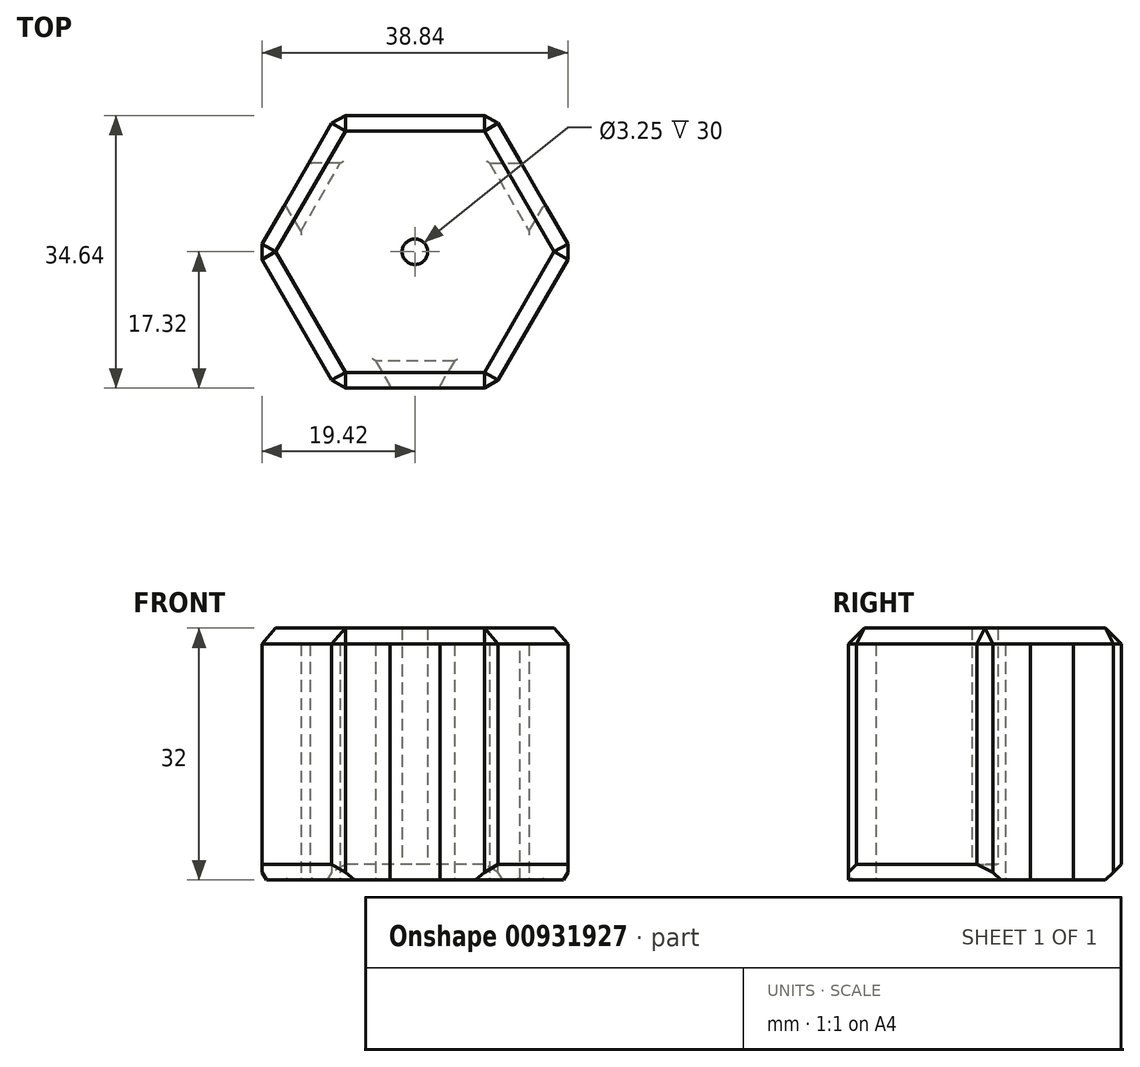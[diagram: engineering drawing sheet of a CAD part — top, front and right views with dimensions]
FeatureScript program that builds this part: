
annotation { "Feature Type Name" : "Feature", "Feature Type Description" : "" }
export const myFeature = defineFeature(function(context is Context, id is Id, definition is map)
    precondition{}
    {
        {
            var Q0;
            Q0=qCreatedBy(makeId("Top.planeOp"),FACE);
            var sketch = newSketch(context, id + "F0", { "sketchPlane" : qUnion([Q0])});
            skCircle(sketch, "E0.cCircle", {"center": v(0, 0) * mm, "radius": 17.32 * mm, "construction": true});
            skLineSegment(sketch, "E0.0", {"start": v(-20, 0) * mm, "end": v(-10, 17.32) * mm});
            skLineSegment(sketch, "E0.1", {"start": v(-10, 17.32) * mm, "end": v(10, 17.32) * mm});
            skLineSegment(sketch, "E0.2", {"start": v(10, 17.32) * mm, "end": v(20, 0) * mm});
            skLineSegment(sketch, "E0.3", {"start": v(20, 0) * mm, "end": v(10, -17.32) * mm});
            skLineSegment(sketch, "E0.4", {"start": v(10, -17.32) * mm, "end": v(-10, -17.32) * mm});
            skLineSegment(sketch, "E0.5", {"start": v(-10, -17.32) * mm, "end": v(-20, 0) * mm});
            skPoint(sketch, "E0.0.midPoint", {"position": v(-15, 8.66) * mm});
            skLineSegment(sketch, "E1", {"start": v(9.5, 11.26) * mm, "end": v(14.5, 2.6) * mm});
            skLineSegment(sketch, "E2", {"start": v(9.5, 11.26) * mm, "end": v(13.5, 11.26) * mm});
            skLineSegment(sketch, "E3", {"start": v(14.5, 2.6) * mm, "end": v(16.5, 6.06) * mm});
            skLineSegment(sketch, "E4", {"start": v(13.5, 11.26) * mm, "end": v(10, 17.32) * mm, "construction": true});
            skLineSegment(sketch, "E5", {"start": v(16.5, 6.06) * mm, "end": v(20, 0) * mm, "construction": true});
            skLineSegment(sketch, "E6.1.0", {"start": v(-9.5, 11.26) * mm, "end": v(-13.5, 11.26) * mm});
            skLineSegment(sketch, "E6.1.1", {"start": v(-14.5, 2.6) * mm, "end": v(-9.5, 11.26) * mm});
            skLineSegment(sketch, "E6.1.2", {"start": v(-14.5, 2.6) * mm, "end": v(-16.5, 6.06) * mm});
            skLineSegment(sketch, "E6.2.0", {"start": v(-5, -13.86) * mm, "end": v(-3, -17.32) * mm});
            skLineSegment(sketch, "E6.2.1", {"start": v(5, -13.86) * mm, "end": v(-5, -13.86) * mm});
            skLineSegment(sketch, "E6.2.2", {"start": v(5, -13.86) * mm, "end": v(3, -17.32) * mm});
            skCircle(sketch, "E7", {"center": v(0, 0) * mm, "radius": 1.63 * mm});
            skSolve(sketch);
        }
        {
            var Q0;
            {var subQ9=sQuery(id+"F0.wireOp",EDGE,"E0.1");Q0=makeQuery(id+"F0.imprint","IMPRINT",FACE,{"disambiguationData":[TD([[makeQuery(id+"F0.imprint","IMPRINT",EDGE,{"derivedFrom":subQ9}),-1.0]])]});}
            extrude(context, id + "F1", {"entities" : qUnion([Q0]), "depth" : 32 * mm, "offsetDistance" : 25 * mm});
        }
        {
            var Q0;
            {var subQ0=sQuery(id+"F0.wireOp",EDGE,"E6.2.0");Q0=makeQuery(id+"F0.imprint","IMPRINT",FACE,{"disambiguationData":[TD([[makeQuery(id+"F0.imprint","IMPRINT",EDGE,{"derivedFrom":subQ0}),1.0]])]});}
            var Q1;
            {var subQ0=sQuery(id+"F0.wireOp",EDGE,"E6.1.0");Q1=makeQuery(id+"F0.imprint","IMPRINT",FACE,{"disambiguationData":[TD([[makeQuery(id+"F0.imprint","IMPRINT",EDGE,{"derivedFrom":subQ0}),1.0]])]});}
            var Q2;
            Q2=makeQuery(id+"F0.imprint","IMPRINT",FACE,{"disambiguationData":[TD([[makeQuery(id+"F0.imprint","IMPRINT",EDGE,{"derivedFrom":sQuery(id+"F0.wireOp",EDGE,"E1")}),1.0]])]});
            extrude(context, id + "F2", {"entities" : qUnion([Q0, Q1, Q2]), "operationType" : NewBodyOperationType.ADD, "depth" : 32 * mm, "offsetDistance" : 25 * mm, "hasSecondDirection" : true, "secondDirectionOppositeDirection" : false, "secondDirectionDepth" : 30 * mm});
        }
        {
            var Q0;
            Q0=makeQuery(id+"F1.opExtrude","CAP_EDGE",EDGE,{"disambiguationData":[OSD([sQuery(id+"F0.wireOp",EDGE,"E0.3")])],"isStart":false});
            var Q1;
            Q1=makeQuery(id+"F1.opExtrude","CAP_EDGE",EDGE,{"disambiguationData":[OSD([sQuery(id+"F0.wireOp",EDGE,"E0.5")])],"isStart":false});
            var Q2;
            Q2=makeQuery(id+"F1.opExtrude","CAP_EDGE",EDGE,{"disambiguationData":[OSD([sQuery(id+"F0.wireOp",EDGE,"E0.1")])],"isStart":false});
            var Q3;
            {var subQ0=sQuery(id+"F0.wireOp",EDGE,"E0.4");Q3=makeQuery(id+"F1.opExtrude","CAP_EDGE",EDGE,{"disambiguationData":[OSD([subQ0]),TDD([makeQuery(id+"F0.imprint","IMPRINT",EDGE,{"disambiguationData":[TD([[makeQuery(id+"F0.imprint","INTERSECT",VERTEX,{"derivedFrom":[subQ0,sQuery(id+"F0.wireOp",EDGE,"E0.5")]}),1.0]])],"derivedFrom":subQ0})])],"isStart":false});}
            var Q4;
            {var subQ0=sQuery(id+"F0.wireOp",EDGE,"E0.4");Q4=makeQuery(id+"F1.opExtrude","CAP_EDGE",EDGE,{"disambiguationData":[OSD([subQ0]),TDD([makeQuery(id+"F0.imprint","IMPRINT",EDGE,{"disambiguationData":[TD([[makeQuery(id+"F0.imprint","INTERSECT",VERTEX,{"derivedFrom":[sQuery(id+"F0.wireOp",EDGE,"E0.3"),subQ0]}),-1.0]])],"derivedFrom":subQ0})])],"isStart":false});}
            var Q5;
            {var subQ0=sQuery(id+"F0.wireOp",EDGE,"E0.2");Q5=makeQuery(id+"F1.opExtrude","CAP_EDGE",EDGE,{"disambiguationData":[OSD([subQ0]),TDD([makeQuery(id+"F0.imprint","IMPRINT",EDGE,{"disambiguationData":[TD([[makeQuery(id+"F0.imprint","INTERSECT",VERTEX,{"derivedFrom":[sQuery(id+"F0.wireOp",EDGE,"E0.1"),subQ0]}),-1.0]])],"derivedFrom":subQ0})])],"isStart":false});}
            var Q6;
            {var subQ0=sQuery(id+"F0.wireOp",EDGE,"E0.0");Q6=makeQuery(id+"F1.opExtrude","CAP_EDGE",EDGE,{"disambiguationData":[OSD([subQ0]),TDD([makeQuery(id+"F0.imprint","IMPRINT",EDGE,{"disambiguationData":[TD([[makeQuery(id+"F0.imprint","INTERSECT",VERTEX,{"derivedFrom":[subQ0,sQuery(id+"F0.wireOp",EDGE,"E0.1")]}),1.0]])],"derivedFrom":subQ0})])],"isStart":false});}
            var Q7;
            {var subQ0=sQuery(id+"F0.wireOp",EDGE,"E0.0");Q7=makeQuery(id+"F1.opExtrude","CAP_EDGE",EDGE,{"disambiguationData":[OSD([subQ0]),TDD([makeQuery(id+"F0.imprint","IMPRINT",EDGE,{"disambiguationData":[TD([[makeQuery(id+"F0.imprint","INTERSECT",VERTEX,{"derivedFrom":[subQ0,sQuery(id+"F0.wireOp",EDGE,"E0.5")]}),-1.0]])],"derivedFrom":subQ0})])],"isStart":false});}
            var Q8;
            {var subQ0=sQuery(id+"F0.wireOp",EDGE,"E7");var subQ1=sQuery(id+"F0.wireOp",EDGE,"E6.2.2");var subQ2=sQuery(id+"F0.wireOp",EDGE,"E6.2.1");var subQ3=sQuery(id+"F0.wireOp",EDGE,"E6.2.0");var subQ4=sQuery(id+"F0.wireOp",EDGE,"E0.4");var subQ5=sQuery(id+"F0.wireOp",EDGE,"E3");var subQ6=sQuery(id+"F0.wireOp",EDGE,"E2");var subQ7=sQuery(id+"F0.wireOp",EDGE,"E1");var subQ8=sQuery(id+"F0.wireOp",EDGE,"E0.2");var subQ9=sQuery(id+"F0.wireOp",EDGE,"E6.1.2");var subQ10=sQuery(id+"F0.wireOp",EDGE,"E6.1.1");var subQ11=sQuery(id+"F0.wireOp",EDGE,"E6.1.0");var subQ12=sQuery(id+"F0.wireOp",EDGE,"E0.0");Q8=makeQuery(id+"F2.boolean.opBoolean","MERGE",FACE,{"derivedFrom":[makeQuery(id+"F1.opExtrude","CAP_FACE",FACE,{"disambiguationData":[OSD([subQ12,sQuery(id+"F0.wireOp",EDGE,"E0.1"),subQ8,sQuery(id+"F0.wireOp",EDGE,"E0.3"),subQ4,sQuery(id+"F0.wireOp",EDGE,"E0.5"),subQ7,subQ6,subQ5,subQ11,subQ10,subQ9,subQ3,subQ2,subQ1,subQ0])],"isStart":true}),makeQuery(id+"F2.opExtrude","CAP_FACE",FACE,{"disambiguationData":[OSD([subQ12,subQ11,subQ10,subQ9])],"isStart":true}),makeQuery(id+"F2.opExtrude","CAP_FACE",FACE,{"disambiguationData":[OSD([subQ8,subQ7,subQ6,subQ5])],"isStart":true}),makeQuery(id+"F2.opExtrude","CAP_FACE",FACE,{"disambiguationData":[OSD([subQ4,subQ3,subQ2,subQ1])],"isStart":true}),makeQuery(id+"F2.opExtrude","CAP_FACE",FACE,{"disambiguationData":[OSD([subQ0])],"isStart":true})]});}
            var Q9;
            Q9=makeQuery(id+"F1.opExtrude","SWEPT_FACE",FACE,{"disambiguationData":[OSD([sQuery(id+"F0.wireOp",EDGE,"E0.5")])]});
            var Q10;
            Q10=makeQuery(id+"F1.opExtrude","SWEPT_FACE",FACE,{"disambiguationData":[OSD([sQuery(id+"F0.wireOp",EDGE,"E0.3")])]});
            var Q11;
            Q11=makeQuery(id+"F1.opExtrude","SWEPT_FACE",FACE,{"disambiguationData":[OSD([sQuery(id+"F0.wireOp",EDGE,"E0.1")])]});
            chamfer(context, id + "F3", {"entities" : qUnion([Q0, Q1, Q2, Q3, Q4, Q5, Q6, Q7, Q8, Q9, Q10, Q11]), "width" : 2 * mm, "tangentPropagation" : true});
        }
        {
            var Q0;
            Q0=makeQuery(id+"F1.opExtrude","SWEPT_EDGE",EDGE,{"disambiguationData":[OSD([sQuery(id+"F0.wireOp",EDGE,"E0.0"),sQuery(id+"F0.wireOp",EDGE,"E6.1.0")])]});
            var Q1;
            Q1=makeQuery(id+"F1.opExtrude","SWEPT_EDGE",EDGE,{"disambiguationData":[OSD([sQuery(id+"F0.wireOp",EDGE,"E0.0"),sQuery(id+"F0.wireOp",EDGE,"E6.1.2")])]});
            var Q2;
            Q2=makeQuery(id+"F1.opExtrude","SWEPT_EDGE",EDGE,{"disambiguationData":[OSD([sQuery(id+"F0.wireOp",EDGE,"E0.4"),sQuery(id+"F0.wireOp",EDGE,"E6.2.2")])]});
            var Q3;
            Q3=makeQuery(id+"F1.opExtrude","SWEPT_EDGE",EDGE,{"disambiguationData":[OSD([sQuery(id+"F0.wireOp",EDGE,"E0.4"),sQuery(id+"F0.wireOp",EDGE,"E6.2.0")])]});
            var Q4;
            Q4=makeQuery(id+"F1.opExtrude","SWEPT_EDGE",EDGE,{"disambiguationData":[OSD([sQuery(id+"F0.wireOp",EDGE,"E0.2"),sQuery(id+"F0.wireOp",EDGE,"E2")])]});
            var Q5;
            Q5=makeQuery(id+"F1.opExtrude","SWEPT_EDGE",EDGE,{"disambiguationData":[OSD([sQuery(id+"F0.wireOp",EDGE,"E0.2"),sQuery(id+"F0.wireOp",EDGE,"E3")])]});
            var Q6;
            Q6=makeQuery(id+"F1.opExtrude","CAP_EDGE",EDGE,{"disambiguationData":[OSD([sQuery(id+"F0.wireOp",EDGE,"E6.2.1")])],"isStart":true});
            var Q7;
            Q7=makeQuery(id+"F1.opExtrude","CAP_EDGE",EDGE,{"disambiguationData":[OSD([sQuery(id+"F0.wireOp",EDGE,"E6.2.0")])],"isStart":true});
            var Q8;
            Q8=makeQuery(id+"F1.opExtrude","CAP_EDGE",EDGE,{"disambiguationData":[OSD([sQuery(id+"F0.wireOp",EDGE,"E6.2.2")])],"isStart":true});
            var Q9;
            Q9=makeQuery(id+"F1.opExtrude","CAP_EDGE",EDGE,{"disambiguationData":[OSD([sQuery(id+"F0.wireOp",EDGE,"E6.1.0")])],"isStart":true});
            var Q10;
            Q10=makeQuery(id+"F1.opExtrude","CAP_EDGE",EDGE,{"disambiguationData":[OSD([sQuery(id+"F0.wireOp",EDGE,"E6.1.1")])],"isStart":true});
            var Q11;
            Q11=makeQuery(id+"F1.opExtrude","CAP_EDGE",EDGE,{"disambiguationData":[OSD([sQuery(id+"F0.wireOp",EDGE,"E6.1.2")])],"isStart":true});
            var Q12;
            Q12=makeQuery(id+"F1.opExtrude","CAP_EDGE",EDGE,{"disambiguationData":[OSD([sQuery(id+"F0.wireOp",EDGE,"E2")])],"isStart":true});
            var Q13;
            Q13=makeQuery(id+"F1.opExtrude","CAP_EDGE",EDGE,{"disambiguationData":[OSD([sQuery(id+"F0.wireOp",EDGE,"E3")])],"isStart":true});
            var Q14;
            Q14=makeQuery(id+"F1.opExtrude","CAP_EDGE",EDGE,{"disambiguationData":[OSD([sQuery(id+"F0.wireOp",EDGE,"E1")])],"isStart":true});
            fillet(context, id + "F4", {"entities" : qUnion([Q0, Q1, Q2, Q3, Q4, Q5, Q6, Q7, Q8, Q9, Q10, Q11, Q12, Q13, Q14]), "radius" : .25 * mm, "tangentPropagation" : true, "allowEdgeOverflow" : false});
        }
        {
            var Q0;
            Q0=makeQuery(id+"F0.imprint","IMPRINT",FACE,{"disambiguationData":[TD([[makeQuery(id+"F0.imprint","IMPRINT",EDGE,{"derivedFrom":sQuery(id+"F0.wireOp",EDGE,"E7")}),1.0]])]});
            extrude(context, id + "F5", {"entities" : qUnion([Q0]), "operationType" : NewBodyOperationType.ADD, "depth" : 2 * mm, "offsetDistance" : 25 * mm});
        }
    });
